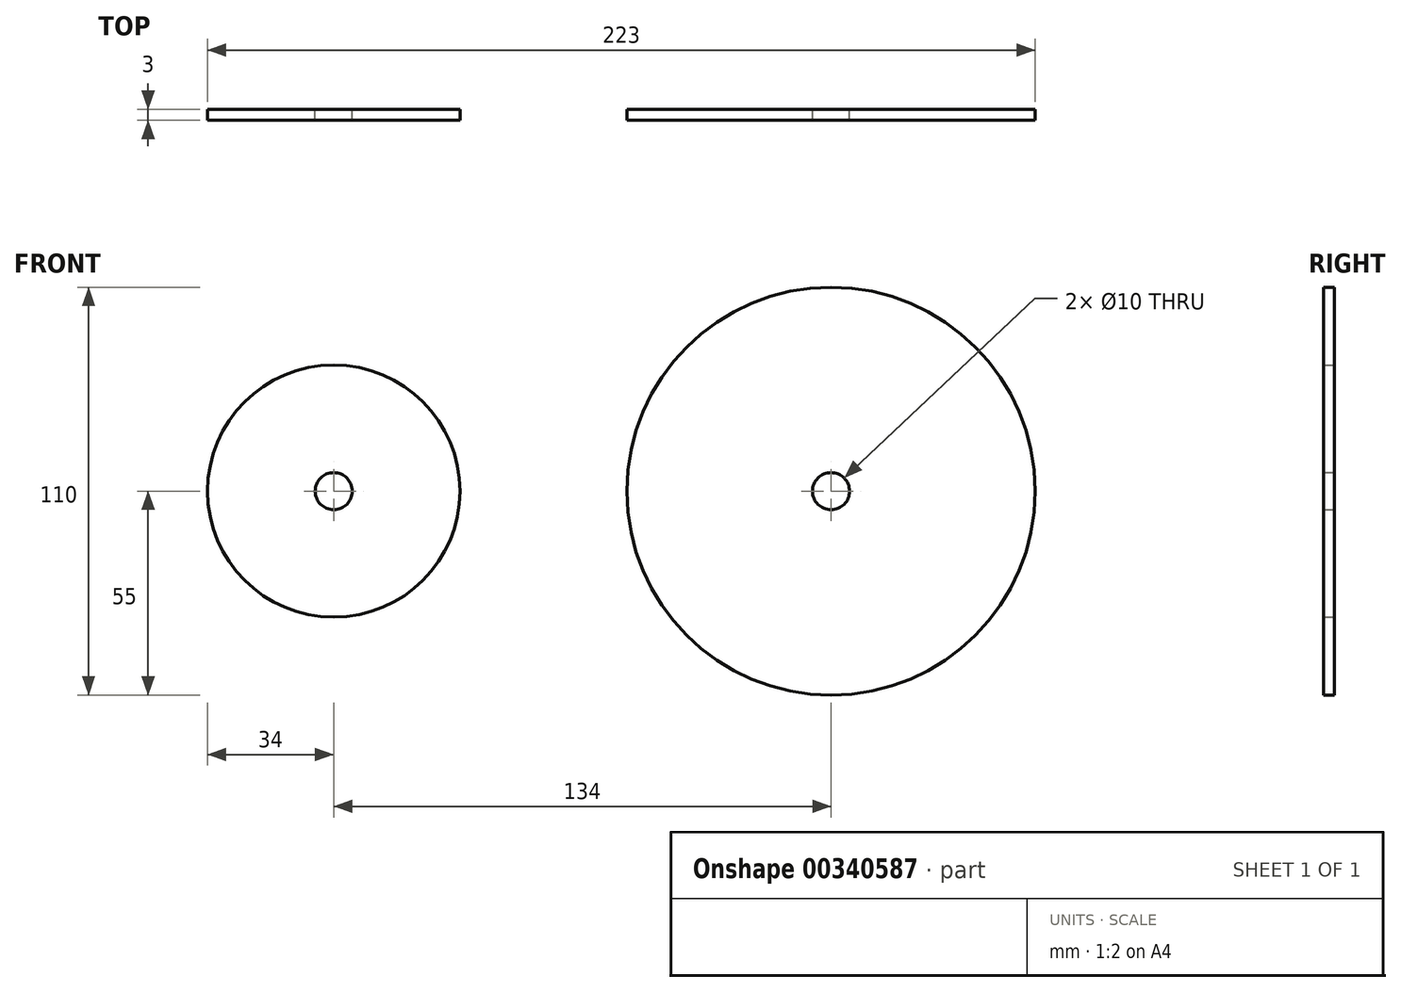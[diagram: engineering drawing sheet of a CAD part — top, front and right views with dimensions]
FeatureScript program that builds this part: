
annotation { "Feature Type Name" : "Feature", "Feature Type Description" : "" }
export const myFeature = defineFeature(function(context is Context, id is Id, definition is map)
    precondition{}
    {
        {
            var Q0;
            Q0=qCreatedBy(makeId("Front.planeOp"),FACE);
            var sketch = newSketch(context, id + "F0", { "sketchPlane" : qUnion([Q0])});
            skCircle(sketch, "E0", {"center": v(0, 0) * mm, "radius": 55 * mm});
            skCircle(sketch, "E1", {"center": v(0, 0) * mm, "radius": 5 * mm});
            skSolve(sketch);
        }
        {
            var Q0;
            Q0=makeQuery(id+"F0.imprint","IMPRINT",FACE,{"disambiguationData":[TD([[makeQuery(id+"F0.imprint","IMPRINT",EDGE,{"derivedFrom":sQuery(id+"F0.wireOp",EDGE,"E0")}),1.0]])]});
            extrude(context, id + "F1", {"entities" : qUnion([Q0]), "depth" : 3 * mm});
        }
        {
            var Q0;
            Q0=qCreatedBy(makeId("Front.planeOp"),FACE);
            var sketch = newSketch(context, id + "F2", { "sketchPlane" : qUnion([Q0])});
            skLineSegment(sketch, "E2", {"start": v(0, 0) * mm, "end": v(-134, 0) * mm, "construction": true});
            skCircle(sketch, "E3", {"center": v(-134, 0) * mm, "radius": 34 * mm});
            skCircle(sketch, "E4", {"center": v(-134, 0) * mm, "radius": 5 * mm});
            skSolve(sketch);
        }
        {
            var Q0;
            Q0=makeQuery(id+"F2.imprint","IMPRINT",FACE,{"disambiguationData":[TD([[makeQuery(id+"F2.imprint","IMPRINT",EDGE,{"derivedFrom":sQuery(id+"F2.wireOp",EDGE,"E3")}),1.0]])]});
            extrude(context, id + "F3", {"entities" : qUnion([Q0]), "depth" : 3 * mm});
        }
    });
